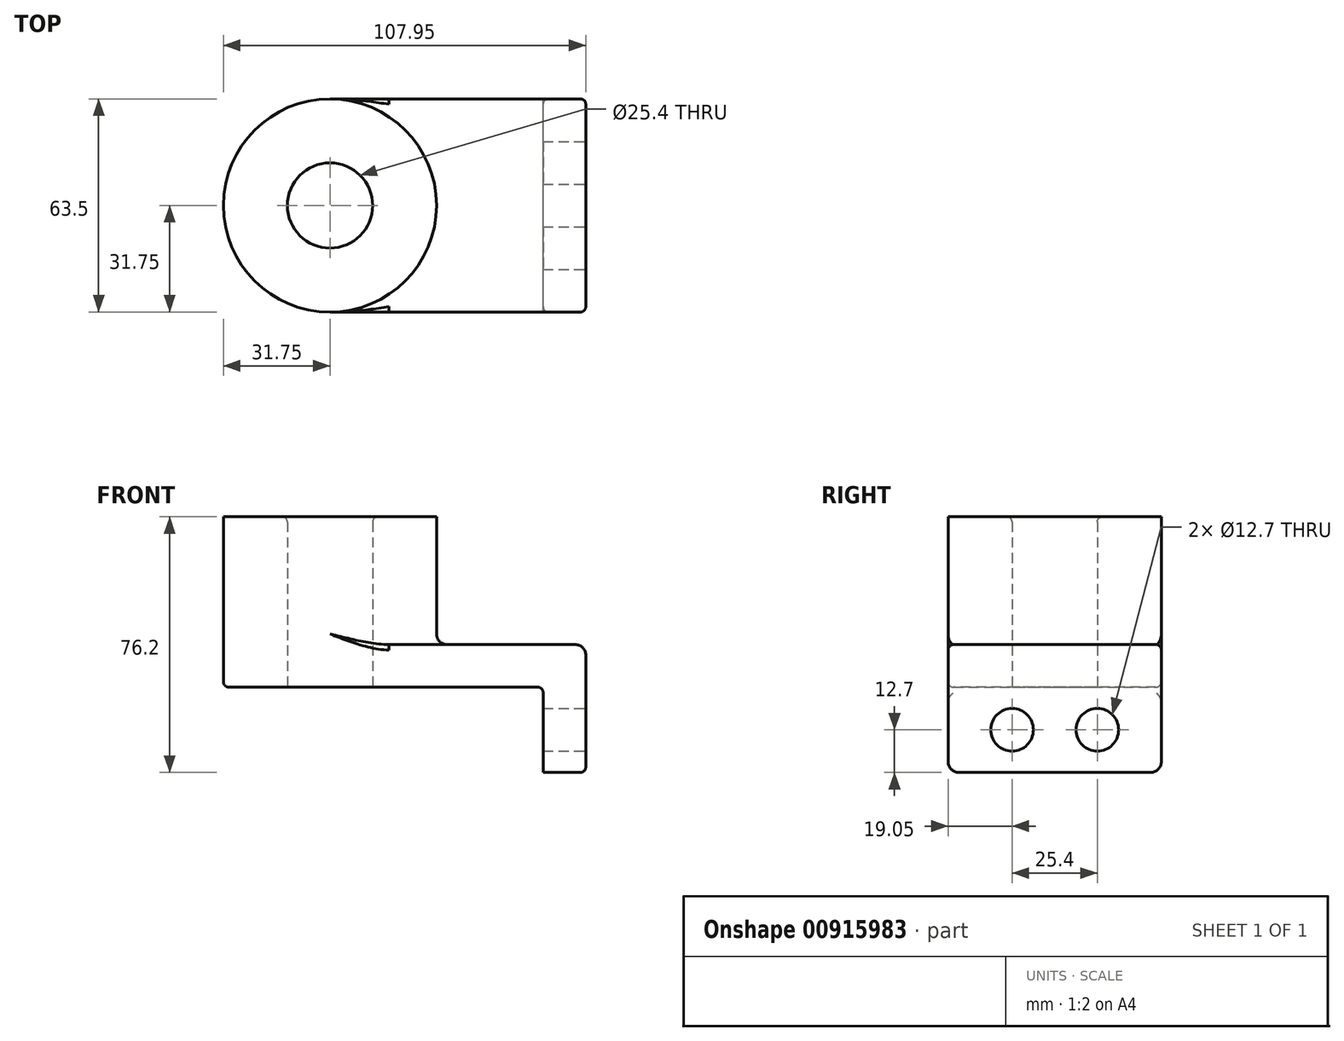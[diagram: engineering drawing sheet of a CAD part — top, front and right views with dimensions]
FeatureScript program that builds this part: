
annotation { "Feature Type Name" : "Feature", "Feature Type Description" : "" }
export const myFeature = defineFeature(function(context is Context, id is Id, definition is map)
    precondition{}
    {
        {
            var Q0;
            Q0=qCreatedBy(makeId("Top.planeOp"),FACE);
            var sketch = newSketch(context, id + "F0", { "sketchPlane" : qUnion([Q0])});
            skLineSegment(sketch, "E0.bottom", {"start": v(38.1, -31.75) * mm, "end": v(-38.1, -31.75) * mm});
            skLineSegment(sketch, "E0.top", {"start": v(38.1, 31.75) * mm, "end": v(-38.1, 31.75) * mm});
            skLineSegment(sketch, "E0.left", {"start": v(38.1, -31.75) * mm, "end": v(38.1, 31.75) * mm});
            skLineSegment(sketch, "E0.right", {"start": v(-38.1, -31.75) * mm, "end": v(-38.1, 31.75) * mm});
            skPoint(sketch, "E0.middle", {"position": v(0, 0) * mm});
            skCircle(sketch, "E1", {"center": v(-38.1, 0) * mm, "radius": 31.75 * mm});
            skCircle(sketch, "E2", {"center": v(-38.1, 0) * mm, "radius": 12.7 * mm});
            skSolve(sketch);
        }
        {
            var Q0;
            Q0 = qSketchRegion(id + "F0", true);
            extrude(context, id + "F1", {"entities" : qUnion([Q0]), "depth" : 12.7 * mm, "offsetDistance" : 25.4 * mm});
        }
        {
            var Q0;
            {var subQ1=sQuery(id+"F0.wireOp",EDGE,"E0.right");var subQ3=sQuery(id+"F0.wireOp",EDGE,"E2");var subQ4=makeQuery(id+"F0.imprint","INTERSECT",VERTEX,{"disambiguationData":[OD(0.0)],"derivedFrom":[subQ1,subQ3]});Q0=makeQuery(id+"F0.imprint","IMPRINT",FACE,{"disambiguationData":[TD([[makeQuery(id+"F0.imprint","IMPRINT",EDGE,{"disambiguationData":[TD([[subQ4,-1.0]])],"derivedFrom":subQ3}),-1.0]])]});}
            var Q1;
            {var subQ1=sQuery(id+"F0.wireOp",EDGE,"E0.right");var subQ3=sQuery(id+"F0.wireOp",EDGE,"E2");var subQ4=makeQuery(id+"F0.imprint","INTERSECT",VERTEX,{"disambiguationData":[OD(0.0)],"derivedFrom":[subQ1,subQ3]});Q1=makeQuery(id+"F0.imprint","IMPRINT",FACE,{"disambiguationData":[TD([[makeQuery(id+"F0.imprint","IMPRINT",EDGE,{"disambiguationData":[TD([[subQ4,1.0]])],"derivedFrom":subQ3}),-1.0]])]});}
            extrude(context, id + "F2", {"entities" : qUnion([Q0, Q1]), "operationType" : NewBodyOperationType.ADD, "depth" : 50.8 * mm, "offsetDistance" : 25.4 * mm});
        }
        {
            var Q0;
            Q0=makeQuery(id+"F1.opExtrude","SWEPT_FACE",FACE,{"disambiguationData":[OSD([sQuery(id+"F0.wireOp",EDGE,"E0.left")])]});
            var sketch = newSketch(context, id + "F3", { "sketchPlane" : qUnion([Q0])});
            skLineSegment(sketch, "E3.bottom", {"start": v(-31.75, 12.7) * mm, "end": v(31.75, 12.7) * mm});
            skLineSegment(sketch, "E3.top", {"start": v(-31.75, -25.4) * mm, "end": v(31.75, -25.4) * mm});
            skLineSegment(sketch, "E3.left", {"start": v(-31.75, 12.7) * mm, "end": v(-31.75, -25.4) * mm});
            skLineSegment(sketch, "E3.right", {"start": v(31.75, 12.7) * mm, "end": v(31.75, -25.4) * mm});
            skCircle(sketch, "E4", {"center": v(-12.7, -12.7) * mm, "radius": 6.35 * mm});
            skLineSegment(sketch, "E5", {"start": v(0, 0) * mm, "end": v(0, -25.4) * mm, "construction": true});
            skCircle(sketch, "E6.MirrorC", {"center": v(12.7, -12.7) * mm, "radius": 6.35 * mm});
            skSolve(sketch);
        }
        {
            var Q0;
            Q0 = qSketchRegion(id + "F3", true);
            extrude(context, id + "F4", {"entities" : qUnion([Q0]), "operationType" : NewBodyOperationType.ADD, "oppositeDirection" : true, "depth" : 12.7 * mm, "offsetDistance" : 25.4 * mm});
        }
        {
            var Q0;
            {var subQ0=sQuery(id+"F0.wireOp",EDGE,"E1");Q0=makeQuery(id+"F2.boolean.opBoolean","INTERSECT",EDGE,{"derivedFrom":[makeQuery(id+"F1.opExtrude","CAP_FACE",FACE,{"disambiguationData":[OSD([sQuery(id+"F0.wireOp",EDGE,"E0.bottom"),sQuery(id+"F0.wireOp",EDGE,"E0.top"),sQuery(id+"F0.wireOp",EDGE,"E0.left"),subQ0,sQuery(id+"F0.wireOp",EDGE,"E2")])],"isStart":false}),makeQuery(id+"F2.opExtrude","SWEPT_FACE",FACE,{"disambiguationData":[OSD([subQ0])]})]});}
            var Q1;
            Q1=makeQuery(id+"F1.opExtrude","CAP_EDGE",EDGE,{"disambiguationData":[OSD([sQuery(id+"F0.wireOp",EDGE,"E0.left")])],"isStart":false});
            var Q2;
            Q2=makeQuery(id+"F4.opExtrude","SWEPT_EDGE",EDGE,{"disambiguationData":[OSD([sQuery(id+"F3.wireOp",EDGE,"E3.top"),sQuery(id+"F3.wireOp",EDGE,"E3.left")])]});
            var Q3;
            Q3=makeQuery(id+"F4.opExtrude","SWEPT_EDGE",EDGE,{"disambiguationData":[OSD([sQuery(id+"F3.wireOp",EDGE,"E3.top"),sQuery(id+"F3.wireOp",EDGE,"E3.right")])]});
            fillet(context, id + "F5", {"entities" : qUnion([Q0, Q1, Q2, Q3]), "radius" : 3.17 * mm, "tangentPropagation" : true, "allowEdgeOverflow" : false});
        }
        {
            var Q0;
            Q0=makeQuery(id+"F1.opExtrude","CAP_EDGE",EDGE,{"disambiguationData":[OSD([sQuery(id+"F0.wireOp",EDGE,"E0.bottom")])],"isStart":false});
            var Q1;
            Q1=makeQuery(id+"F1.opExtrude","CAP_EDGE",EDGE,{"disambiguationData":[OSD([sQuery(id+"F0.wireOp",EDGE,"E0.bottom")])],"isStart":true});
            var Q2;
            Q2=makeQuery(id+"F1.opExtrude","CAP_EDGE",EDGE,{"disambiguationData":[OSD([sQuery(id+"F0.wireOp",EDGE,"E0.top")])],"isStart":false});
            var Q3;
            Q3=makeQuery(id+"F2.opExtrude","CAP_EDGE",EDGE,{"disambiguationData":[OSD([sQuery(id+"F0.wireOp",EDGE,"E2")])],"isStart":false});
            var Q4;
            Q4=makeQuery(id+"F4.boolean.opBoolean","INTERSECT",EDGE,{"derivedFrom":[makeQuery(id+"F1.opExtrude","CAP_FACE",FACE,{"disambiguationData":[OSD([sQuery(id+"F0.wireOp",EDGE,"E0.bottom"),sQuery(id+"F0.wireOp",EDGE,"E0.top"),sQuery(id+"F0.wireOp",EDGE,"E0.left"),sQuery(id+"F0.wireOp",EDGE,"E1"),sQuery(id+"F0.wireOp",EDGE,"E2")])],"isStart":true}),makeQuery(id+"F4.opExtrude","CAP_FACE",FACE,{"disambiguationData":[OSD([sQuery(id+"F3.wireOp",EDGE,"E3.bottom"),sQuery(id+"F3.wireOp",EDGE,"E3.top"),sQuery(id+"F3.wireOp",EDGE,"E3.left"),sQuery(id+"F3.wireOp",EDGE,"E3.right"),sQuery(id+"F3.wireOp",EDGE,"E4"),sQuery(id+"F3.wireOp",EDGE,"E6.MirrorC")])],"isStart":false})]});
            fillet(context, id + "F6", {"entities" : qUnion([Q0, Q1, Q2, Q3, Q4]), "radius" : 1.59 * mm, "tangentPropagation" : true, "allowEdgeOverflow" : false});
        }
    });
